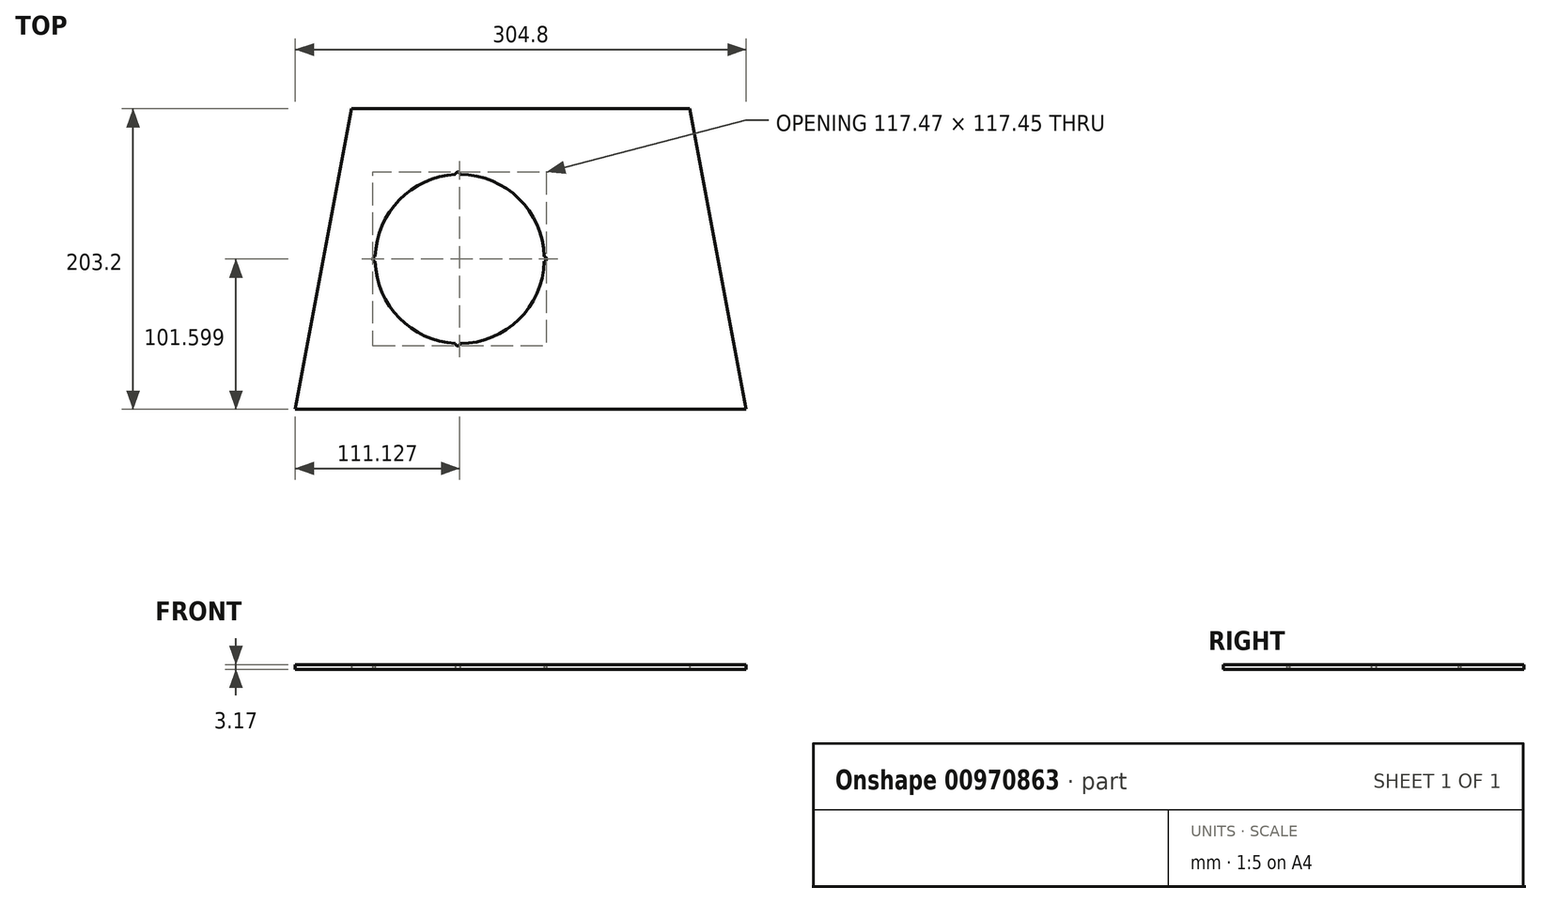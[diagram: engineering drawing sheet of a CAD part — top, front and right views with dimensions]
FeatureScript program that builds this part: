
annotation { "Feature Type Name" : "Feature", "Feature Type Description" : "" }
export const myFeature = defineFeature(function(context is Context, id is Id, definition is map)
    precondition{}
    {
        {
            var Q0;
            Q0=qCreatedBy(makeId("Top.planeOp"),FACE);
            var sketch = newSketch(context, id + "F0", { "sketchPlane" : qUnion([Q0])});
            skLineSegment(sketch, "E0", {"start": v(-146.43, -20.57) * mm, "end": v(158.37, -20.57) * mm});
            skLineSegment(sketch, "E1", {"start": v(5.97, 182.63) * mm, "end": v(120.27, 182.63) * mm});
            skLineSegment(sketch, "E2.MirrorCS", {"start": v(5.97, 182.63) * mm, "end": v(-108.33, 182.63) * mm});
            skLineSegment(sketch, "E3", {"start": v(-108.33, 182.63) * mm, "end": v(-146.43, -20.57) * mm});
            skLineSegment(sketch, "E4", {"start": v(158.37, -20.57) * mm, "end": v(120.27, 182.63) * mm});
            skCircle(sketch, "E5", {"center": v(-35.3, 81.03) * mm, "radius": 57.15 * mm});
            skLineSegment(sketch, "E6", {"start": v(-92.45, 81.03) * mm, "end": v(21.85, 81.03) * mm});
            skLineSegment(sketch, "E7", {"start": v(-35.3, 138.18) * mm, "end": v(-35.3, 23.88) * mm});
            skSolve(sketch);
        }
        {
            var Q0;
            Q0=makeQuery(id+"F0.imprint","IMPRINT",FACE,{"disambiguationData":[TD([[makeQuery(id+"F0.imprint","IMPRINT",EDGE,{"derivedFrom":sQuery(id+"F0.wireOp",EDGE,"E0")}),1.0]])]});
            extrude(context, id + "F1", {"entities" : qUnion([Q0]), "depth" : 3.17 * mm, "offsetDistance" : 25.4 * mm});
        }
        {
            var Q0;
            Q0=makeQuery(id+"F1.opExtrude","CAP_FACE",FACE,{"disambiguationData":[OSD([sQuery(id+"F0.wireOp",EDGE,"E0"),sQuery(id+"F0.wireOp",EDGE,"E1"),sQuery(id+"F0.wireOp",EDGE,"E2.MirrorCS"),sQuery(id+"F0.wireOp",EDGE,"E3"),sQuery(id+"F0.wireOp",EDGE,"E4"),sQuery(id+"F0.wireOp",EDGE,"E5")])],"isStart":false});
            var sketch = newSketch(context, id + "F2", { "sketchPlane" : qUnion([Q0])});
            skLineSegment(sketch, "E8", {"start": v(-36.54, 138.17) * mm, "end": v(-36.54, 23.9) * mm});
            skLineSegment(sketch, "E9", {"start": v(-36.54, 23.9) * mm, "end": v(21.85, 81.03) * mm});
            skPoint(sketch, "E9.endSnap0", {"position": v(-36.54, 81.03) * mm});
            skLineSegment(sketch, "E10", {"start": v(-92.45, 81.03) * mm, "end": v(21.85, 81.03) * mm});
            skPoint(sketch, "E11", {"position": v(-36.54, 138.17) * mm});
            skPoint(sketch, "E12", {"position": v(21.85, 81.03) * mm});
            skPoint(sketch, "E13", {"position": v(-92.45, 81.03) * mm});
            skPoint(sketch, "E14", {"position": v(-36.54, 23.9) * mm});
            skSolve(sketch);
        }
        {
            var Q0;
            Q0=sQuery(id+"F2.wireOp",VERTEX,"E11");
            var Q1;
            Q1=sQuery(id+"F2.wireOp",VERTEX,"E12");
            var Q2;
            Q2=sQuery(id+"F2.wireOp",VERTEX,"E14");
            var Q3;
            Q3=sQuery(id+"F2.wireOp",VERTEX,"E13");
            var Q4;
            Q4=makeQuery(id+"F1.opExtrude","SWEPT_BODY",BODY,{"disambiguationData":[OSD([sQuery(id+"F0.wireOp",EDGE,"E0"),sQuery(id+"F0.wireOp",EDGE,"E1"),sQuery(id+"F0.wireOp",EDGE,"E2.MirrorCS"),sQuery(id+"F0.wireOp",EDGE,"E3"),sQuery(id+"F0.wireOp",EDGE,"E4"),sQuery(id+"F0.wireOp",EDGE,"E5")])]});
            hole(context, id + "F3", {"style" : HoleStyle.SIMPLE, "endStyle" : HoleEndStyle.BLIND, "holeDiameter" : 3.17 * mm, "majorDiameter" : 6.35 * mm, "holeDepth" : 17.46 * mm, "tappedDepth" : 12.7 * mm, "tapClearance" : 3, "locations" : qUnion([Q0, Q1, Q2, Q3]), "scope" : qUnion([Q4]), "startStyle" : HoleStartStyle.SKETCH});
        }
    });
